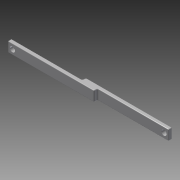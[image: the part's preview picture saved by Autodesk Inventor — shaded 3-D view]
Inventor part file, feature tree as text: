
AUTODESK INVENTOR PART (.ipt)
format: ipt  version: 2013 (Build 170138000, 138)  size: 145,920 bytes
history: native  units: in
note: dims shown in document units (in); Inventor stores cm internally (conversion verified against a paired STEP export)
features: fillet x3, extrude x2, sketch x2
ambient origin geometry x8: Origin, YZ Plane, XZ Plane, XY Plane, X Axis, Y Axis, Z Axis, Center Point
bodies: Solid1 (feature_tree)
feature tree (7):
  extrude  "Extrusion1"  Depth=1.0in
  extrude  "Extrusion2"  Depth=0.45in
  fillet  "Fillet1"  Radius=0.5in
  fillet  "Fillet2"  Radius=0.5in
  fillet  "Fillet3"  Radius=0.7in
  sketch  "Sketch1"  dims[d0=15.5in d1=1.0in]
  sketch  "Sketch2"  dims[d2=0.45in d3=0.45in d4=0.5in d5=0.5in d6=0.7in d7=0.0in d8=7.0in d9=2.0in d10=0.0in d11=0.125in d12=0.0625in d13=0.0125in]
